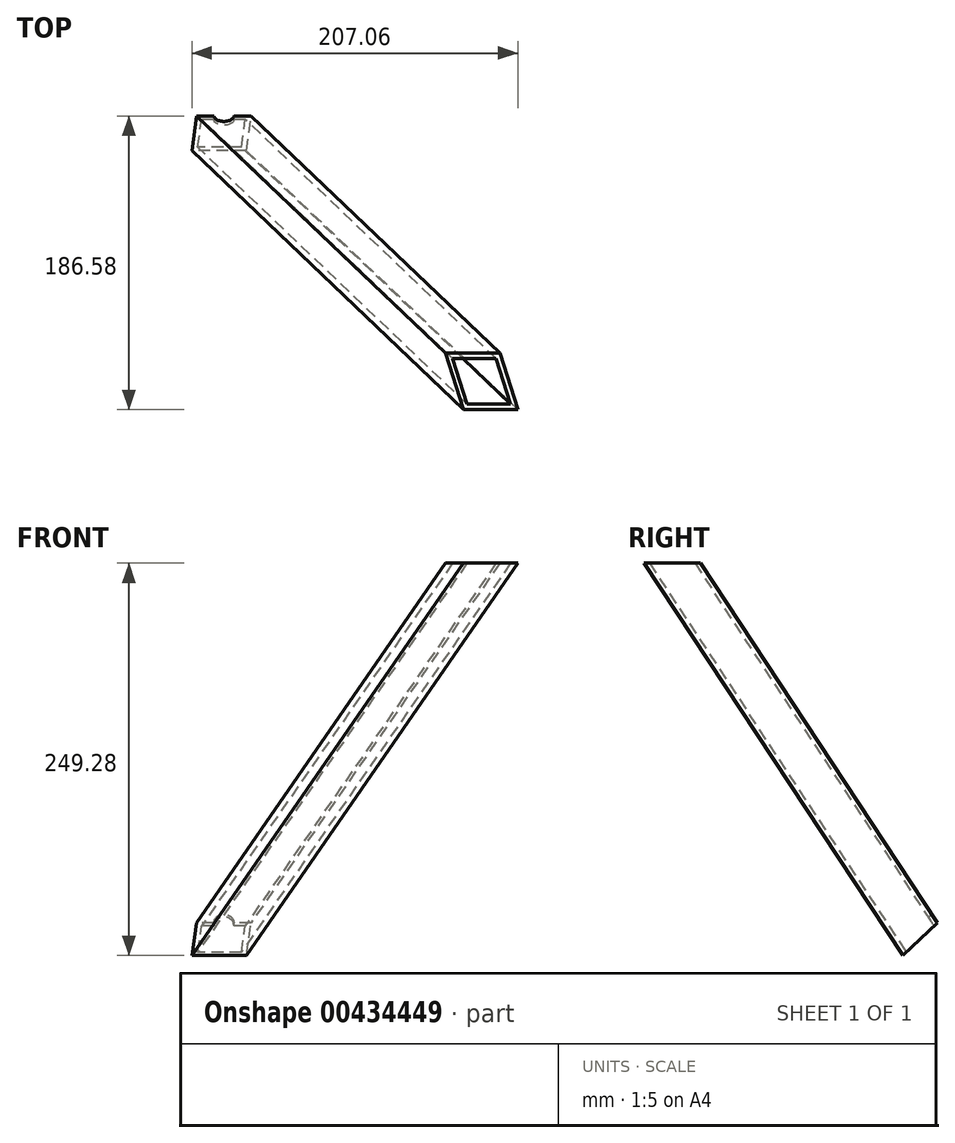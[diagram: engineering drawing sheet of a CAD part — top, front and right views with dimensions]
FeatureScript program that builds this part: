
annotation { "Feature Type Name" : "Feature", "Feature Type Description" : "" }
export const myFeature = defineFeature(function(context is Context, id is Id, definition is map)
    precondition{}
    {
        {
            var Q0;
            Q0=qCreatedBy(makeId("Top.planeOp"),FACE);
            var sketch = newSketch(context, id + "F0", { "sketchPlane" : qUnion([Q0])});
            skLineSegment(sketch, "E0", {"start": v(-60.5, 0) * mm, "end": v(74.21, 0) * mm, "construction": true});
            skLineSegment(sketch, "E1", {"start": v(0, 0) * mm, "end": v(0, 96.14) * mm, "construction": true});
            skSolve(sketch);
        }
        {
            var Q0;
            Q0=qCreatedBy(makeId("Top.planeOp"),FACE);
            var Q1;
            Q1=sQuery(id+"F0.wireOp",EDGE,"E0");
            cPlane(context, id + "F1", {"entities" : qUnion([Q0, Q1]), "cplaneType" : CPlaneType.LINE_ANGLE, "offset" : 25 * mm, "angle" : 33.41 * degree, "width" : 150 * mm, "height" : 150 * mm});
        }
        {
            var Q0;
            Q0=qCreatedBy(id+"F1.planeOp",FACE);
            var sketch = newSketch(context, id + "F2", { "sketchPlane" : qUnion([Q0])});
            skLineSegment(sketch, "E2", {"start": v(0, 0) * mm, "end": v(0, 75.9) * mm, "construction": true});
            skSolve(sketch);
        }
        {
            var Q0;
            Q0=sQuery(id+"F2.wireOp",EDGE,"E2");
            var Q1;
            Q1=qCreatedBy(id+"F1.planeOp",FACE);
            cPlane(context, id + "F3", {"entities" : qUnion([Q0, Q1]), "cplaneType" : CPlaneType.LINE_ANGLE, "offset" : 25 * mm, "angle" : 30 * degree, "oppositeDirection" : true, "width" : 150 * mm, "height" : 150 * mm});
        }
        {
            var Q0;
            Q0=qCreatedBy(id+"F3.planeOp",FACE);
            var sketch = newSketch(context, id + "F4", { "sketchPlane" : qUnion([Q0])});
            skLineSegment(sketch, "E3.bottom", {"start": v(15, -15) * mm, "end": v(-15, -15) * mm});
            skLineSegment(sketch, "E3.top", {"start": v(15, 15) * mm, "end": v(-15, 15) * mm});
            skLineSegment(sketch, "E3.left", {"start": v(15, -15) * mm, "end": v(15, 15) * mm});
            skLineSegment(sketch, "E3.right", {"start": v(-15, -15) * mm, "end": v(-15, 15) * mm});
            skPoint(sketch, "E3.middle", {"position": v(0, 0) * mm});
            skLineSegment(sketch, "E4.bottom", {"start": v(12, -12) * mm, "end": v(-12, -12) * mm});
            skLineSegment(sketch, "E4.top", {"start": v(12, 12) * mm, "end": v(-12, 12) * mm});
            skLineSegment(sketch, "E4.left", {"start": v(12, -12) * mm, "end": v(12, 12) * mm});
            skLineSegment(sketch, "E4.right", {"start": v(-12, -12) * mm, "end": v(-12, 12) * mm});
            skSolve(sketch);
        }
        {
            var Q0;
            Q0 = qSketchRegion(id + "F4", true);
            extrude(context, id + "F5", {"entities" : qUnion([Q0]), "depth" : 1000 * mm, "offsetDistance" : 25 * mm});
        }
        {
            var Q0;
            Q0=qCreatedBy(makeId("Top.planeOp"),FACE);
            cPlane(context, id + "F6", {"entities" : qUnion([Q0]), "cplaneType" : CPlaneType.OFFSET, "offset" : 260 * mm, "width" : 150 * mm, "height" : 150 * mm});
        }
        {
            var Q0;
            Q0=qCreatedBy(id+"F6.planeOp",FACE);
            var sketch = newSketch(context, id + "F7", { "sketchPlane" : qUnion([Q0])});
            skLineSegment(sketch, "E5.bottom", {"start": v(1189.75, 475.45) * mm, "end": v(-170.15, 475.45) * mm});
            skLineSegment(sketch, "E5.top", {"start": v(1189.75, -986.8) * mm, "end": v(-170.15, -986.8) * mm});
            skLineSegment(sketch, "E5.left", {"start": v(1189.75, 475.45) * mm, "end": v(1189.75, -986.8) * mm});
            skLineSegment(sketch, "E5.right", {"start": v(-170.15, 475.45) * mm, "end": v(-170.15, -986.8) * mm});
            skPoint(sketch, "E5.middle", {"position": v(509.8, -255.68) * mm});
            skSolve(sketch);
        }
        {
            var Q0;
            Q0 = qSketchRegion(id + "F7", true);
            extrude(context, id + "F8", {"entities" : qUnion([Q0]), "operationType" : NewBodyOperationType.REMOVE, "endBound" : BoundingType.THROUGH_ALL, "depth" : 25 * mm, "offsetDistance" : 25 * mm});
        }
        {
            var Q0;
            Q0=qCreatedBy(id+"F1.planeOp",FACE);
            var Q1;
            Q1=sQuery(id+"F0.wireOp",EDGE,"E0");
            cPlane(context, id + "F9", {"entities" : qUnion([Q0, Q1]), "cplaneType" : CPlaneType.LINE_ANGLE, "offset" : 25 * mm, "angle" : 10 * degree, "width" : 150 * mm, "height" : 150 * mm});
        }
        {
            var Q0;
            Q0=qCreatedBy(id+"F9.planeOp",FACE);
            cPlane(context, id + "F10", {"entities" : qUnion([Q0]), "cplaneType" : CPlaneType.OFFSET, "offset" : 25 * mm, "width" : 150 * mm, "height" : 150 * mm});
        }
        {
            var Q0;
            Q0=qCreatedBy(id+"F10.planeOp",FACE);
            var sketch = newSketch(context, id + "F11", { "sketchPlane" : qUnion([Q0])});
            skLineSegment(sketch, "E6.bottom", {"start": v(-130.4, -114.3) * mm, "end": v(130.4, -114.3) * mm});
            skLineSegment(sketch, "E6.top", {"start": v(-130.4, 114.3) * mm, "end": v(130.4, 114.3) * mm});
            skLineSegment(sketch, "E6.left", {"start": v(-130.4, -114.3) * mm, "end": v(-130.4, 114.3) * mm});
            skLineSegment(sketch, "E6.right", {"start": v(130.4, -114.3) * mm, "end": v(130.4, 114.3) * mm});
            skPoint(sketch, "E6.middle", {"position": v(0, 0) * mm});
            skSolve(sketch);
        }
        {
            var Q0;
            Q0 = qSketchRegion(id + "F11", true);
            extrude(context, id + "F12", {"entities" : qUnion([Q0]), "operationType" : NewBodyOperationType.REMOVE, "endBound" : BoundingType.THROUGH_ALL, "oppositeDirection" : true, "depth" : 25 * mm, "offsetDistance" : 25 * mm});
        }
        {
            var Q0;
            Q0=makeQuery(id+"F5.opExtrude","SWEPT_FACE",FACE,{"disambiguationData":[OSD([sQuery(id+"F4.wireOp",EDGE,"E3.top")])]});
            var sketch = newSketch(context, id + "F13", { "sketchPlane" : qUnion([Q0])});
            skCircle(sketch, "E7", {"center": v(-16.18, 28.03) * mm, "radius": 6.31 * mm});
            skSolve(sketch);
        }
        {
            var Q0;
            Q0 = qSketchRegion(id + "F13", true);
            var Q1;
            Q1=makeQuery(id+"F5.opExtrude","SWEPT_FACE",FACE,{"disambiguationData":[OSD([sQuery(id+"F4.wireOp",EDGE,"E4.top")])]});
            extrude(context, id + "F14", {"entities" : qUnion([Q0]), "operationType" : NewBodyOperationType.REMOVE, "endBound" : BoundingType.UP_TO_SURFACE, "oppositeDirection" : true, "depth" : 25 * mm, "endBoundEntityFace" : qUnion([Q1]), "offsetDistance" : 25 * mm});
        }
    });
